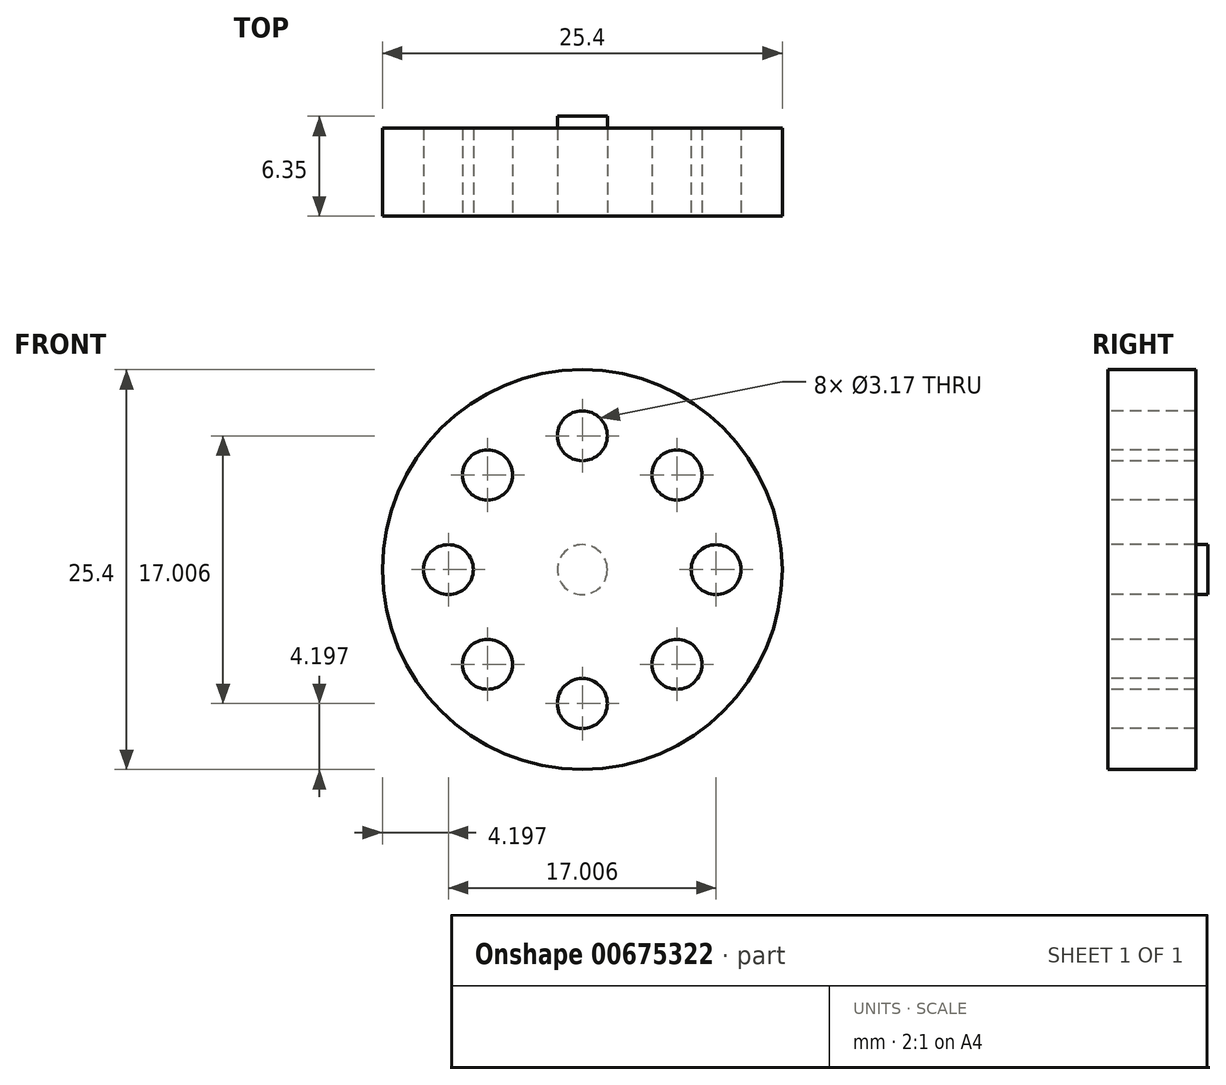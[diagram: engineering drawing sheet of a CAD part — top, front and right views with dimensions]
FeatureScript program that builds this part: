
annotation { "Feature Type Name" : "Feature", "Feature Type Description" : "" }
export const myFeature = defineFeature(function(context is Context, id is Id, definition is map)
    precondition{}
    {
        {
            var Q0;
            Q0=qCreatedBy(makeId("Front.planeOp"),FACE);
            var sketch = newSketch(context, id + "F0", { "sketchPlane" : qUnion([Q0])});
            skCircle(sketch, "E0", {"center": v(0, 0) * mm, "radius": 15.88 * mm});
            skCircle(sketch, "E1", {"center": v(0, 0) * mm, "radius": 12.7 * mm});
            skCircle(sketch, "E2", {"center": v(0, 8.5) * mm, "radius": 1.59 * mm});
            skCircle(sketch, "E3.1.0", {"center": v(-6.01, 6.01) * mm, "radius": 1.59 * mm});
            skCircle(sketch, "E3.2.0", {"center": v(-8.5, 0) * mm, "radius": 1.59 * mm});
            skCircle(sketch, "E3.3.0", {"center": v(-6.01, -6.01) * mm, "radius": 1.59 * mm});
            skCircle(sketch, "E3.4.0", {"center": v(0, -8.5) * mm, "radius": 1.59 * mm});
            skCircle(sketch, "E3.5.0", {"center": v(6.01, -6.01) * mm, "radius": 1.59 * mm});
            skCircle(sketch, "E3.6.0", {"center": v(8.5, 0) * mm, "radius": 1.59 * mm});
            skCircle(sketch, "E3.7.0", {"center": v(6.01, 6.01) * mm, "radius": 1.59 * mm});
            skCircle(sketch, "E4", {"center": v(0, 0) * mm, "radius": 6.35 * mm});
            skCircle(sketch, "E5", {"center": v(0, 0) * mm, "radius": 3.18 * mm});
            skSolve(sketch);
        }
        {
            var Q0;
            Q0=makeQuery(id+"F0.imprint","IMPRINT",FACE,{"disambiguationData":[TD([[makeQuery(id+"F0.imprint","IMPRINT",EDGE,{"derivedFrom":sQuery(id+"F0.wireOp",EDGE,"E1")}),1.0]])]});
            var Q1;
            Q1=makeQuery(id+"F0.imprint","IMPRINT",FACE,{"disambiguationData":[TD([[makeQuery(id+"F0.imprint","IMPRINT",EDGE,{"derivedFrom":sQuery(id+"F0.wireOp",EDGE,"E5")}),1.0]])]});
            var Q2;
            Q2=makeQuery(id+"F0.imprint","IMPRINT",FACE,{"disambiguationData":[TD([[makeQuery(id+"F0.imprint","IMPRINT",EDGE,{"derivedFrom":sQuery(id+"F0.wireOp",EDGE,"E4")}),1.0]])]});
            extrude(context, id + "F1", {"entities" : qUnion([Q0, Q1, Q2]), "oppositeDirection" : true, "depth" : 5.6 * mm, "offsetDistance" : 25.4 * mm});
        }
        {
            var Q0;
            Q0=qCreatedBy(makeId("Front.planeOp"),FACE);
            var sketch = newSketch(context, id + "F2", { "sketchPlane" : qUnion([Q0])});
            skCircle(sketch, "E6", {"center": v(0, 0) * mm, "radius": 1.59 * mm});
            skSolve(sketch);
        }
        {
            var Q0;
            Q0=makeQuery(id+"F2.imprint","IMPRINT",FACE,{"disambiguationData":[TD([[makeQuery(id+"F2.imprint","IMPRINT",EDGE,{"derivedFrom":sQuery(id+"F2.wireOp",EDGE,"E6")}),1.0]])]});
            extrude(context, id + "F3", {"entities" : qUnion([Q0]), "operationType" : NewBodyOperationType.ADD, "oppositeDirection" : true, "depth" : 6.35 * mm, "offsetDistance" : 25.4 * mm});
        }
    });
